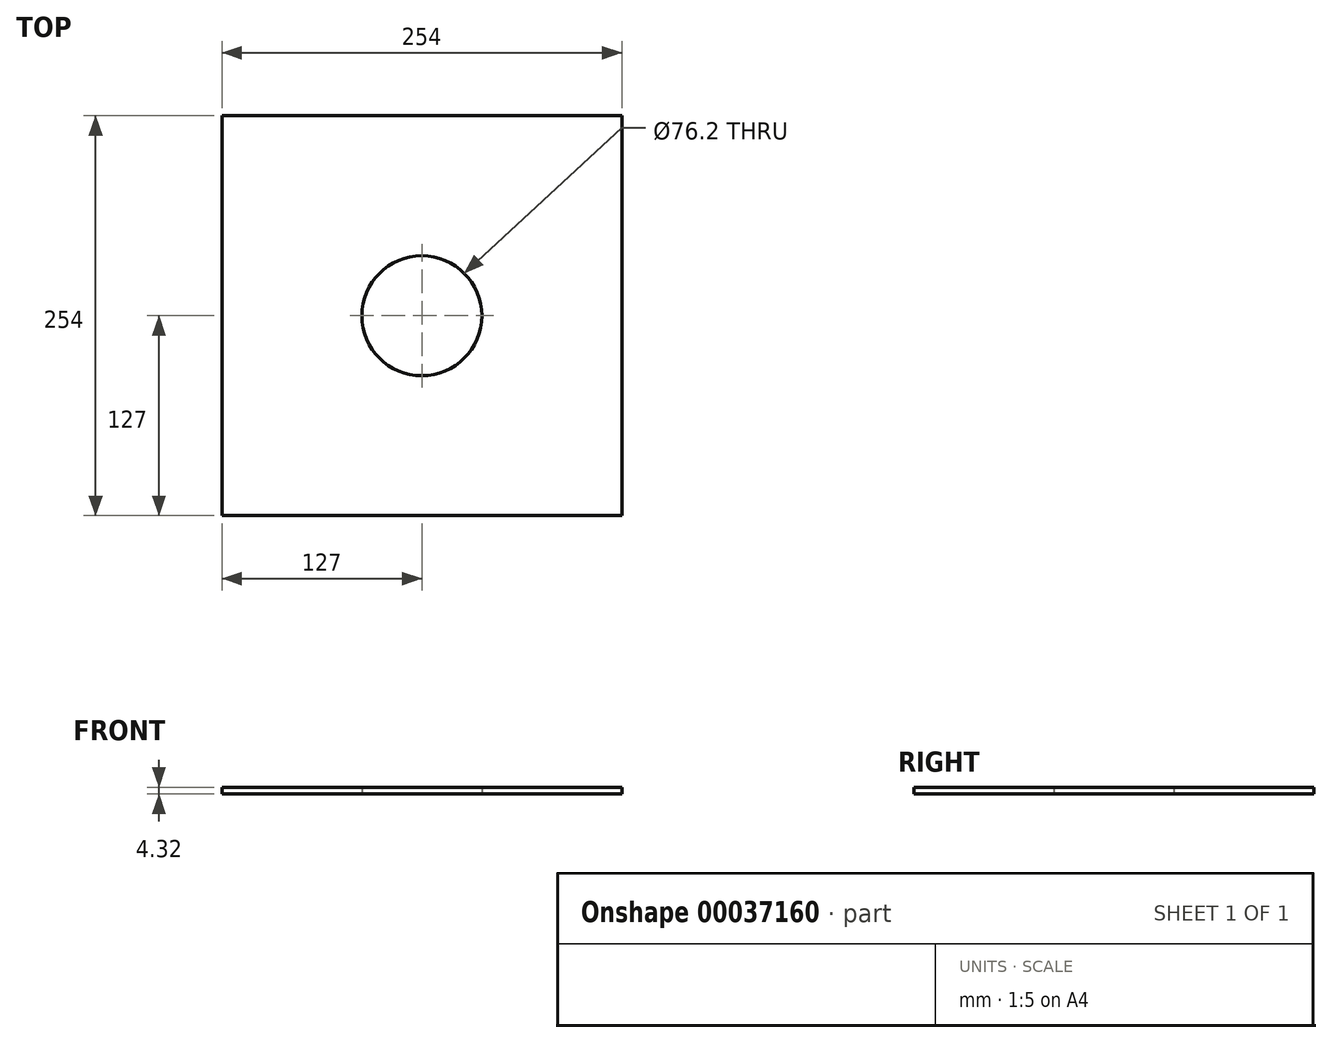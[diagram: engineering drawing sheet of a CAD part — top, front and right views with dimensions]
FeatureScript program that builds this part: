
annotation { "Feature Type Name" : "Feature", "Feature Type Description" : "" }
export const myFeature = defineFeature(function(context is Context, id is Id, definition is map)
    precondition{}
    {
        {
            var Q0;
            Q0=qCreatedBy(makeId("Top.planeOp"),FACE);
            var sketch = newSketch(context, id + "F0", { "sketchPlane" : qUnion([Q0])});
            skLineSegment(sketch, "E0.rect.bottom", {"start": v(-127, 127) * mm, "end": v(127, 127) * mm});
            skLineSegment(sketch, "E0.rect.top", {"start": v(-127, -127) * mm, "end": v(127, -127) * mm});
            skLineSegment(sketch, "E0.rect.left", {"start": v(-127, 127) * mm, "end": v(-127, -127) * mm});
            skLineSegment(sketch, "E0.rect.right", {"start": v(127, 127) * mm, "end": v(127, -127) * mm});
            skPoint(sketch, "E0.rect.middle", {"position": v(0, 0) * mm});
            skCircle(sketch, "E1", {"center": v(0, 0) * mm, "radius": 38.1 * mm});
            skSolve(sketch);
        }
        {
            var Q0;
            Q0=makeQuery(id+"F0.imprint","IMPRINT",FACE,{"disambiguationData":[TD([[makeQuery(id+"F0.imprint","IMPRINT",EDGE,{"derivedFrom":sQuery(id+"F0.wireOp",EDGE,"E0.rect.bottom")}),-1.0]])]});
            extrude(context, id + "F1", {"entities" : qUnion([Q0]), "depth" : 4.32 * mm});
        }
    });
